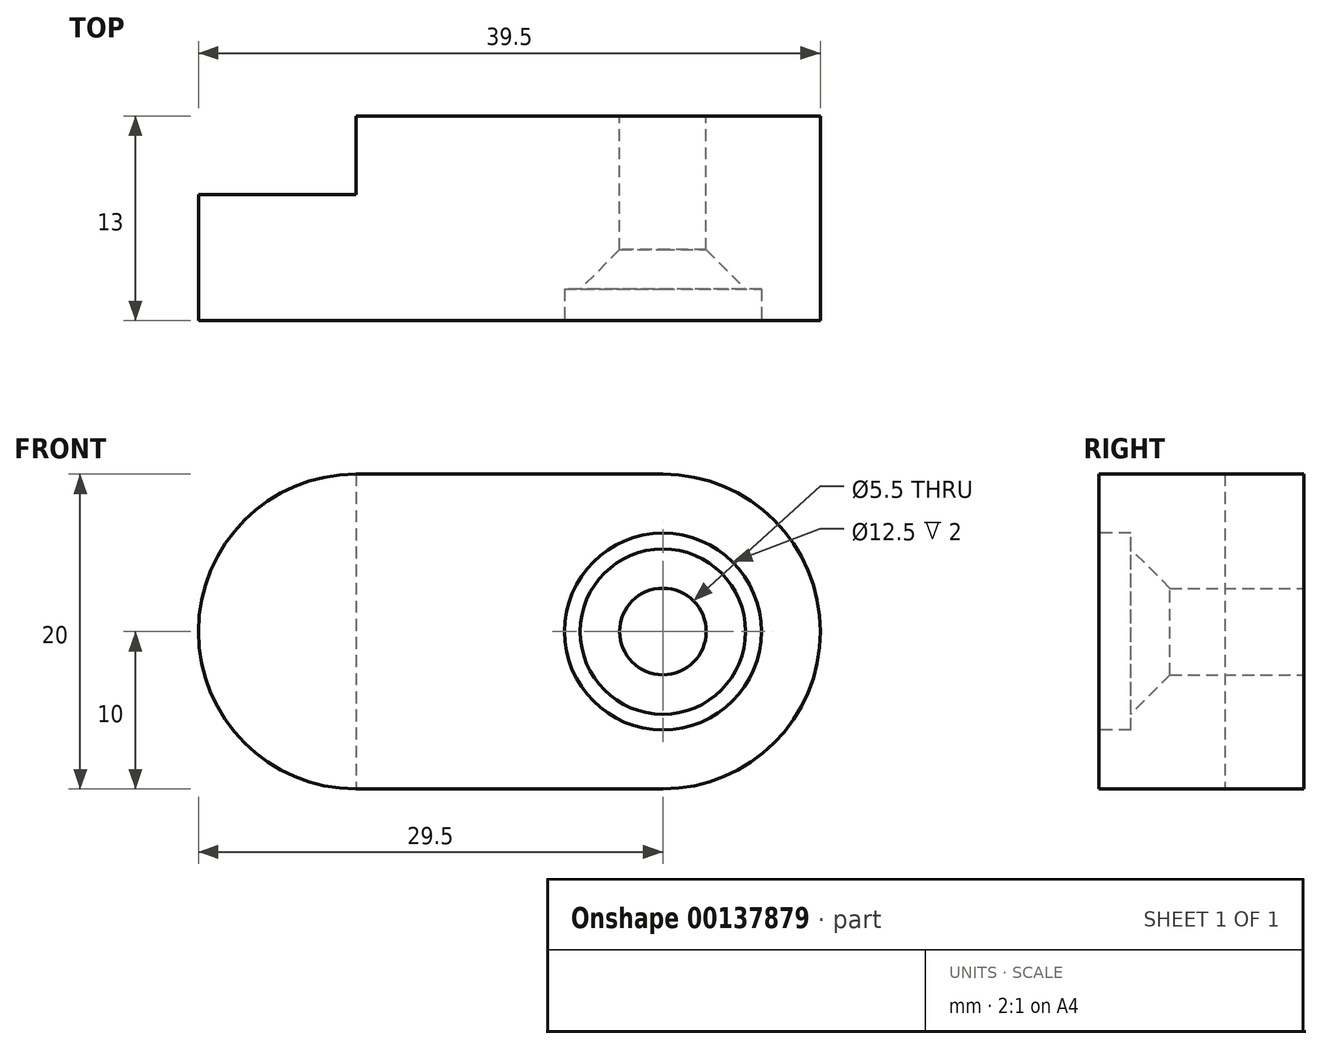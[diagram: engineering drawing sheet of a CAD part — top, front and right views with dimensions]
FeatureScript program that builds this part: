
annotation { "Feature Type Name" : "Feature", "Feature Type Description" : "" }
export const myFeature = defineFeature(function(context is Context, id is Id, definition is map)
    precondition{}
    {
        {
            var Q0;
            Q0=qCreatedBy(makeId("Front.planeOp"),FACE);
            var sketch = newSketch(context, id + "F0", { "sketchPlane" : qUnion([Q0])});
            skCircle(sketch, "E0", {"center": v(0, 0) * mm, "radius": 2.75 * mm});
            skArc(sketch, "E1", {"start": v(0, 10) * mm, "mid": v(10, 0) * mm, "end": v(0, -10) * mm});
            skLineSegment(sketch, "E2", {"start": v(0, 10) * mm, "end": v(-19.5, 10) * mm});
            skLineSegment(sketch, "E3.MirrorCS", {"start": v(0, -10) * mm, "end": v(-19.5, -10) * mm});
            skLineSegment(sketch, "E4", {"start": v(-19.5, 10) * mm, "end": v(-19.5, -10) * mm});
            skSolve(sketch);
        }
        {
            var Q0;
            Q0 = qSketchRegion(id + "F0", true);
            extrude(context, id + "F1", {"entities" : qUnion([Q0]), "depth" : 5 * mm});
        }
        {
            var Q0;
            Q0=makeQuery(id+"F1.opExtrude","CAP_FACE",FACE,{"disambiguationData":[OSD([sQuery(id+"F0.wireOp",EDGE,"E0"),sQuery(id+"F0.wireOp",EDGE,"E1"),sQuery(id+"F0.wireOp",EDGE,"E2"),sQuery(id+"F0.wireOp",EDGE,"E3.MirrorCS"),sQuery(id+"F0.wireOp",EDGE,"E4")])],"isStart":false});
            var sketch = newSketch(context, id + "F2", { "sketchPlane" : qUnion([Q0])});
            skLineSegment(sketch, "E5.0", {"start": v(0, 10) * mm, "end": v(-19.5, 10) * mm});
            skArc(sketch, "E6.0", {"start": v(0, 10) * mm, "mid": v(10, 0) * mm, "end": v(0, -10) * mm});
            skCircle(sketch, "E7.0", {"center": v(0, 0) * mm, "radius": 2.75 * mm});
            skLineSegment(sketch, "E8.0", {"start": v(0, -10) * mm, "end": v(-19.5, -10) * mm});
            skArc(sketch, "E9", {"start": v(-19.5, 10) * mm, "mid": v(-29.5, 0) * mm, "end": v(-19.5, -10) * mm});
            skSolve(sketch);
        }
        {
            var Q0;
            Q0 = qSketchRegion(id + "F2", true);
            extrude(context, id + "F3", {"entities" : qUnion([Q0]), "operationType" : NewBodyOperationType.ADD, "depth" : 8 * mm});
        }
        {
            var Q0;
            Q0=makeQuery(id+"F3.opExtrude","CAP_FACE",FACE,{"disambiguationData":[OSD([sQuery(id+"F2.wireOp",EDGE,"E5.0"),sQuery(id+"F2.wireOp",EDGE,"E6.0"),sQuery(id+"F2.wireOp",EDGE,"E7.0"),sQuery(id+"F2.wireOp",EDGE,"E8.0"),sQuery(id+"F2.wireOp",EDGE,"E9")])],"isStart":false});
            var sketch = newSketch(context, id + "F4", { "sketchPlane" : qUnion([Q0])});
            skCircle(sketch, "E10", {"center": v(0, 0) * mm, "radius": 6.25 * mm});
            skSolve(sketch);
        }
        {
            var Q0;
            Q0 = qSketchRegion(id + "F4", true);
            extrude(context, id + "F5", {"entities" : qUnion([Q0]), "operationType" : NewBodyOperationType.REMOVE, "oppositeDirection" : true, "depth" : 2 * mm});
        }
        {
            var Q0;
            Q0=makeQuery(id+"F5.boolean.opBoolean","INTERSECT",EDGE,{"derivedFrom":[makeQuery(id+"F3.boolean.opBoolean","MERGE",FACE,{"derivedFrom":[makeQuery(id+"F1.opExtrude","SWEPT_FACE",FACE,{"disambiguationData":[OSD([sQuery(id+"F0.wireOp",EDGE,"E0")])]}),makeQuery(id+"F3.opExtrude","SWEPT_FACE",FACE,{"disambiguationData":[OSD([sQuery(id+"F2.wireOp",EDGE,"E7.0")])]})]}),makeQuery(id+"F5.opExtrude","CAP_FACE",FACE,{"disambiguationData":[OSD([sQuery(id+"F4.wireOp",EDGE,"E10")])],"isStart":false})]});
            chamfer(context, id + "F6", {"entities" : qUnion([Q0]), "width" : 2.5 * mm, "tangentPropagation" : true});
        }
    });
